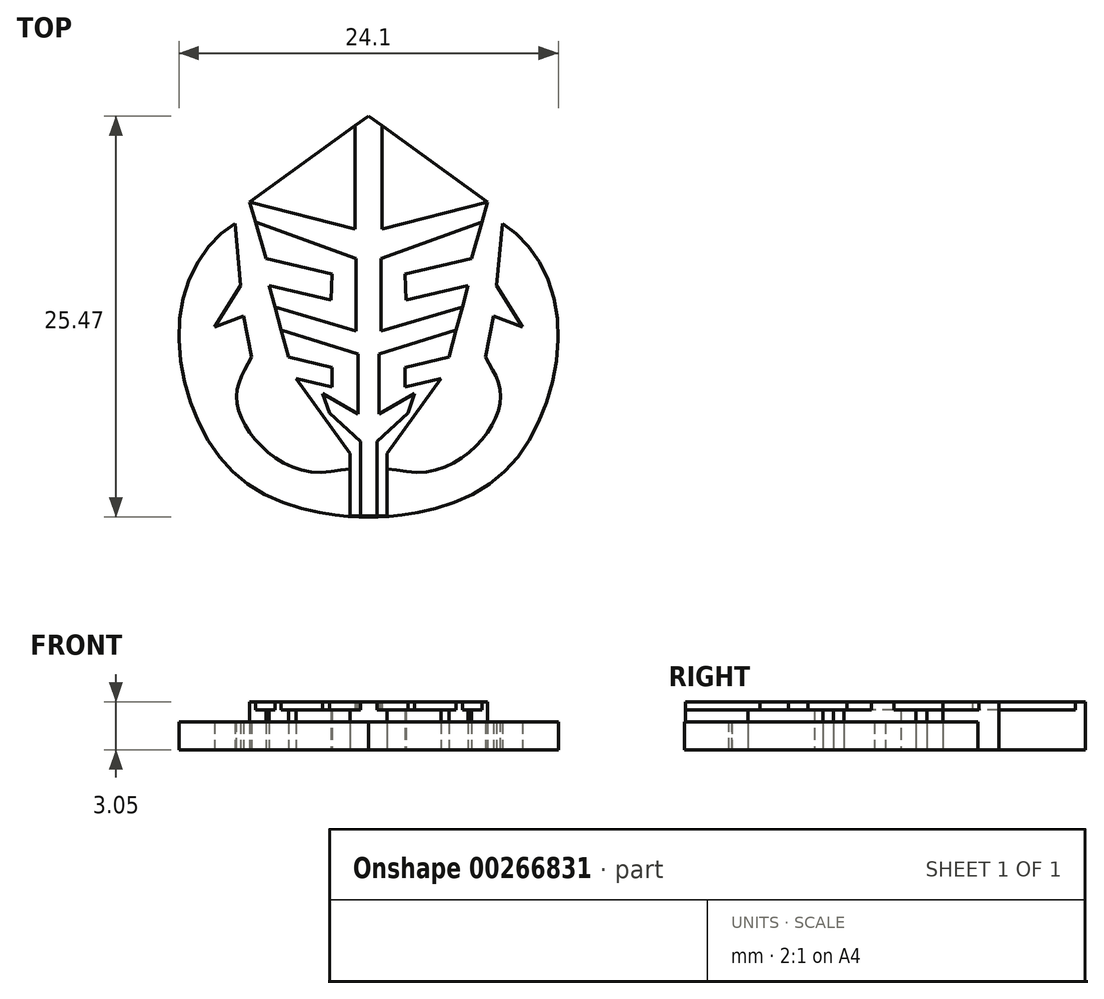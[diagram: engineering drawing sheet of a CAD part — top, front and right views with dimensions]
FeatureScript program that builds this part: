
annotation { "Feature Type Name" : "Feature", "Feature Type Description" : "" }
export const myFeature = defineFeature(function(context is Context, id is Id, definition is map)
    precondition{}
    {
        {
            var Q0;
            Q0=qCreatedBy(makeId("Top.planeOp"),FACE);
            var sketch = newSketch(context, id + "F0", { "sketchPlane" : qUnion([Q0])});
            skLineSegment(sketch, "E0.bottom", {"start": v(-12.7, 12.7) * mm, "end": v(12.7, 12.7) * mm, "construction": true});
            skLineSegment(sketch, "E0.top", {"start": v(-12.7, -12.7) * mm, "end": v(12.7, -12.7) * mm, "construction": true});
            skLineSegment(sketch, "E0.left", {"start": v(-12.7, 12.7) * mm, "end": v(-12.7, -12.7) * mm, "construction": true});
            skLineSegment(sketch, "E0.right", {"start": v(12.7, 12.7) * mm, "end": v(12.7, -12.7) * mm, "construction": true});
            skPoint(sketch, "E0.middle", {"position": v(0, 0) * mm});
            skLineSegment(sketch, "E1", {"start": v(0, 12.7) * mm, "end": v(-7.55, 7.22) * mm});
            skLineSegment(sketch, "E2", {"start": v(-7.55, 7.22) * mm, "end": v(-6.52, 3.64) * mm});
            skLineSegment(sketch, "E3", {"start": v(-6.52, 3.64) * mm, "end": v(-2.3, 2.64) * mm});
            skLineSegment(sketch, "E4", {"start": v(-6.33, 1.94) * mm, "end": v(-5.1, -2.62) * mm});
            skLineSegment(sketch, "E5", {"start": v(-5.1, -2.62) * mm, "end": v(-2.3, -3.29) * mm});
            skLineSegment(sketch, "E6", {"start": v(-2.3, -3.29) * mm, "end": v(-2.3, -4.51) * mm});
            skLineSegment(sketch, "E7", {"start": v(-2.3, -4.51) * mm, "end": v(-4.6, -3.97) * mm});
            skLineSegment(sketch, "E8", {"start": v(-4.6, -3.97) * mm, "end": v(-1.17, -8.73) * mm});
            skLineSegment(sketch, "E9", {"start": v(-1.17, -8.73) * mm, "end": v(-1.17, -12.7) * mm});
            skLineSegment(sketch, "E10", {"start": v(-1.17, -12.7) * mm, "end": v(0, -12.7) * mm});
            skLineSegment(sketch, "E11", {"start": v(0, 12.7) * mm, "end": v(0, -12.7) * mm, "construction": true});
            skLineSegment(sketch, "E12", {"start": v(-6.33, 1.94) * mm, "end": v(-2.38, 1) * mm});
            skLineSegment(sketch, "E13", {"start": v(-2.38, 1) * mm, "end": v(-2.3, 2.64) * mm});
            skLineSegment(sketch, "E14.MirrorCS", {"start": v(0, 12.7) * mm, "end": v(7.55, 7.22) * mm});
            skLineSegment(sketch, "E15.MirrorCS", {"start": v(7.55, 7.22) * mm, "end": v(6.52, 3.64) * mm});
            skLineSegment(sketch, "E16.MirrorCS", {"start": v(6.52, 3.64) * mm, "end": v(2.3, 2.64) * mm});
            skLineSegment(sketch, "E17.MirrorCS", {"start": v(2.38, 1) * mm, "end": v(2.3, 2.64) * mm});
            skLineSegment(sketch, "E18.MirrorCS", {"start": v(6.33, 1.94) * mm, "end": v(2.38, 1) * mm});
            skLineSegment(sketch, "E19.MirrorCS", {"start": v(6.33, 1.94) * mm, "end": v(5.1, -2.62) * mm});
            skLineSegment(sketch, "E20.MirrorCS", {"start": v(5.1, -2.62) * mm, "end": v(2.3, -3.29) * mm});
            skLineSegment(sketch, "E21.MirrorCS", {"start": v(2.3, -3.29) * mm, "end": v(2.3, -4.51) * mm});
            skLineSegment(sketch, "E22.MirrorCS", {"start": v(2.3, -4.51) * mm, "end": v(4.6, -3.97) * mm});
            skLineSegment(sketch, "E23.MirrorCS", {"start": v(4.6, -3.97) * mm, "end": v(1.17, -8.73) * mm});
            skLineSegment(sketch, "E24.MirrorCS", {"start": v(1.17, -8.73) * mm, "end": v(1.17, -12.7) * mm});
            skLineSegment(sketch, "E25.MirrorCS", {"start": v(1.17, -12.7) * mm, "end": v(0, -12.7) * mm});
            skSolve(sketch);
        }
        {
            var Q0;
            Q0 = qSketchRegion(id + "F0", true);
            extrude(context, id + "F1", {"entities" : qUnion([Q0]), "depth" : 2.54 * mm});
        }
        {
            var Q0;
            Q0=makeQuery(id+"F1.opExtrude","CAP_FACE",FACE,{"disambiguationData":[OSD([sQuery(id+"F0.wireOp",EDGE,"E1"),sQuery(id+"F0.wireOp",EDGE,"E2"),sQuery(id+"F0.wireOp",EDGE,"E3"),sQuery(id+"F0.wireOp",EDGE,"E4"),sQuery(id+"F0.wireOp",EDGE,"E5"),sQuery(id+"F0.wireOp",EDGE,"E6"),sQuery(id+"F0.wireOp",EDGE,"E7"),sQuery(id+"F0.wireOp",EDGE,"E8"),sQuery(id+"F0.wireOp",EDGE,"E9"),sQuery(id+"F0.wireOp",EDGE,"E10"),sQuery(id+"F0.wireOp",EDGE,"E12"),sQuery(id+"F0.wireOp",EDGE,"E13"),sQuery(id+"F0.wireOp",EDGE,"E14.MirrorCS"),sQuery(id+"F0.wireOp",EDGE,"E15.MirrorCS"),sQuery(id+"F0.wireOp",EDGE,"E16.MirrorCS"),sQuery(id+"F0.wireOp",EDGE,"E17.MirrorCS"),sQuery(id+"F0.wireOp",EDGE,"E18.MirrorCS"),sQuery(id+"F0.wireOp",EDGE,"E19.MirrorCS"),sQuery(id+"F0.wireOp",EDGE,"E20.MirrorCS"),sQuery(id+"F0.wireOp",EDGE,"E21.MirrorCS"),sQuery(id+"F0.wireOp",EDGE,"E22.MirrorCS"),sQuery(id+"F0.wireOp",EDGE,"E23.MirrorCS"),sQuery(id+"F0.wireOp",EDGE,"E24.MirrorCS"),sQuery(id+"F0.wireOp",EDGE,"E25.MirrorCS")])],"isStart":false});
            var sketch = newSketch(context, id + "F2", { "sketchPlane" : qUnion([Q0])});
            skLineSegment(sketch, "E26", {"start": v(-7.55, 7.22) * mm, "end": v(-0.86, 5.52) * mm});
            skLineSegment(sketch, "E27", {"start": v(0, 12.7) * mm, "end": v(0, -12.7) * mm});
            skLineSegment(sketch, "E28", {"start": v(0, -12.7) * mm, "end": v(-0.53, -12.7) * mm});
            skLineSegment(sketch, "E29", {"start": v(-0.53, -12.7) * mm, "end": v(-0.53, -7.97) * mm});
            skLineSegment(sketch, "E30", {"start": v(-0.53, -7.97) * mm, "end": v(-2.5, -6.16) * mm});
            skLineSegment(sketch, "E31", {"start": v(-2.93, -4.93) * mm, "end": v(-0.68, -6.23) * mm});
            skLineSegment(sketch, "E32", {"start": v(-0.68, -6.23) * mm, "end": v(-0.68, -2.43) * mm});
            skLineSegment(sketch, "E33", {"start": v(-0.68, -2.43) * mm, "end": v(-5.56, -0.9) * mm});
            skLineSegment(sketch, "E34", {"start": v(-5.95, 0.55) * mm, "end": v(-0.8, -0.96) * mm});
            skLineSegment(sketch, "E35", {"start": v(-0.8, -0.96) * mm, "end": v(-0.8, 3.64) * mm});
            skLineSegment(sketch, "E36", {"start": v(-0.8, 3.64) * mm, "end": v(-7.19, 5.95) * mm});
            skLineSegment(sketch, "E37.MirrorCS", {"start": v(7.55, 7.22) * mm, "end": v(0.86, 5.52) * mm});
            skLineSegment(sketch, "E38.MirrorCS", {"start": v(0.8, 3.64) * mm, "end": v(7.19, 5.95) * mm});
            skLineSegment(sketch, "E39.MirrorCS", {"start": v(0.8, -0.96) * mm, "end": v(0.8, 3.64) * mm});
            skLineSegment(sketch, "E40.MirrorCS", {"start": v(5.95, 0.55) * mm, "end": v(0.8, -0.96) * mm});
            skLineSegment(sketch, "E41.MirrorCS", {"start": v(0.68, -2.43) * mm, "end": v(5.56, -0.9) * mm});
            skLineSegment(sketch, "E42.MirrorCS", {"start": v(0.68, -6.23) * mm, "end": v(0.68, -2.43) * mm});
            skLineSegment(sketch, "E43.MirrorCS", {"start": v(2.93, -4.93) * mm, "end": v(0.68, -6.23) * mm});
            skLineSegment(sketch, "E44.MirrorCS", {"start": v(0.53, -7.97) * mm, "end": v(2.5, -6.16) * mm});
            skLineSegment(sketch, "E45.MirrorCS", {"start": v(0.53, -12.7) * mm, "end": v(0.53, -7.97) * mm});
            skLineSegment(sketch, "E46.MirrorCS", {"start": v(0, -12.7) * mm, "end": v(0.53, -12.7) * mm});
            skLineSegment(sketch, "E47", {"start": v(-2.5, -6.16) * mm, "end": v(-2.93, -4.93) * mm});
            skLineSegment(sketch, "E48", {"start": v(2.93, -4.93) * mm, "end": v(2.5, -6.16) * mm});
            skLineSegment(sketch, "E49", {"start": v(-5.56, -0.9) * mm, "end": v(-5.95, 0.55) * mm});
            skLineSegment(sketch, "E50", {"start": v(-7.55, 7.22) * mm, "end": v(-7.19, 5.95) * mm});
            skLineSegment(sketch, "E51", {"start": v(7.55, 7.22) * mm, "end": v(7.19, 5.95) * mm});
            skLineSegment(sketch, "E52", {"start": v(5.95, 0.55) * mm, "end": v(5.56, -0.9) * mm});
            skLineSegment(sketch, "E53", {"start": v(-0.86, 5.52) * mm, "end": v(-0.86, 12.08) * mm});
            skLineSegment(sketch, "E54", {"start": v(-0.86, 12.08) * mm, "end": v(0, 12.7) * mm});
            skLineSegment(sketch, "E55", {"start": v(0.85, 12.08) * mm, "end": v(0.86, 5.52) * mm});
            skLineSegment(sketch, "E56", {"start": v(0, 12.7) * mm, "end": v(0.85, 12.08) * mm});
            skSolve(sketch);
        }
        {
            var Q0;
            Q0 = qSketchRegion(id + "F2", true);
            extrude(context, id + "F3", {"entities" : qUnion([Q0]), "operationType" : NewBodyOperationType.ADD, "depth" : 0.5 * mm});
        }
        {
            var Q0;
            Q0=qCreatedBy(makeId("Top.planeOp"),FACE);
            var sketch = newSketch(context, id + "F4", { "sketchPlane" : qUnion([Q0])});
            skFitSpline(sketch, "E57", {"points": [v(0, -12.76) * mm, v(-2, -12.67) * mm, v(-7.33, -10.93) * mm, v(-11.22, -5.72) * mm, v(-11.7, 1.44) * mm, v(-8.5, 5.87) * mm], "startDerivative": vector(-13.52, -0.23) * mm, "endDerivative": vector(20.35, 12.78) * mm});
            skFitSpline(sketch, "E58", {"points": [v(0, -12.76) * mm, v(-2.9, -9.93) * mm, v(-7.03, -8.04) * mm, v(-8.38, -5.07) * mm, v(-7.42, -2.62) * mm], "startDerivative": vector(4.4, 44.6) * mm, "endDerivative": vector(6.55, 11) * mm});
            skLineSegment(sketch, "E59", {"start": v(-8.5, 5.87) * mm, "end": v(-8.12, 1.93) * mm});
            skLineSegment(sketch, "E60", {"start": v(-8.12, 1.93) * mm, "end": v(-9.78, -0.7) * mm});
            skLineSegment(sketch, "E61", {"start": v(-9.78, -0.7) * mm, "end": v(-7.94, 0) * mm});
            skLineSegment(sketch, "E62", {"start": v(-7.94, 0) * mm, "end": v(-7.42, -2.62) * mm});
            skLineSegment(sketch, "E63", {"start": v(0, 0) * mm, "end": v(0, -12.76) * mm});
            skFitSpline(sketch, "E64.MirrorCS", {"points": [v(0, -12.76) * mm, v(2.9, -9.93) * mm, v(7.03, -8.04) * mm, v(8.38, -5.07) * mm, v(7.42, -2.62) * mm], "startDerivative": vector(-4.4, 44.6) * mm, "endDerivative": vector(-6.55, 11) * mm});
            skLineSegment(sketch, "E65.MirrorCS", {"start": v(7.94, 0) * mm, "end": v(7.42, -2.62) * mm});
            skLineSegment(sketch, "E66.MirrorCS", {"start": v(9.78, -0.7) * mm, "end": v(7.94, 0) * mm});
            skLineSegment(sketch, "E67.MirrorCS", {"start": v(8.12, 1.93) * mm, "end": v(9.78, -0.7) * mm});
            skLineSegment(sketch, "E68.MirrorCS", {"start": v(8.5, 5.87) * mm, "end": v(8.12, 1.93) * mm});
            skFitSpline(sketch, "E69.MirrorCS", {"points": [v(0, -12.76) * mm, v(2, -12.67) * mm, v(7.33, -10.93) * mm, v(11.22, -5.72) * mm, v(11.7, 1.44) * mm, v(8.5, 5.87) * mm], "startDerivative": vector(13.52, -0.23) * mm, "endDerivative": vector(-20.35, 12.78) * mm});
            skSolve(sketch);
        }
        {
            var Q0;
            Q0 = qSketchRegion(id + "F4", true);
            extrude(context, id + "F5", {"entities" : qUnion([Q0]), "operationType" : NewBodyOperationType.ADD, "depth" : 1.78 * mm});
        }
    });
